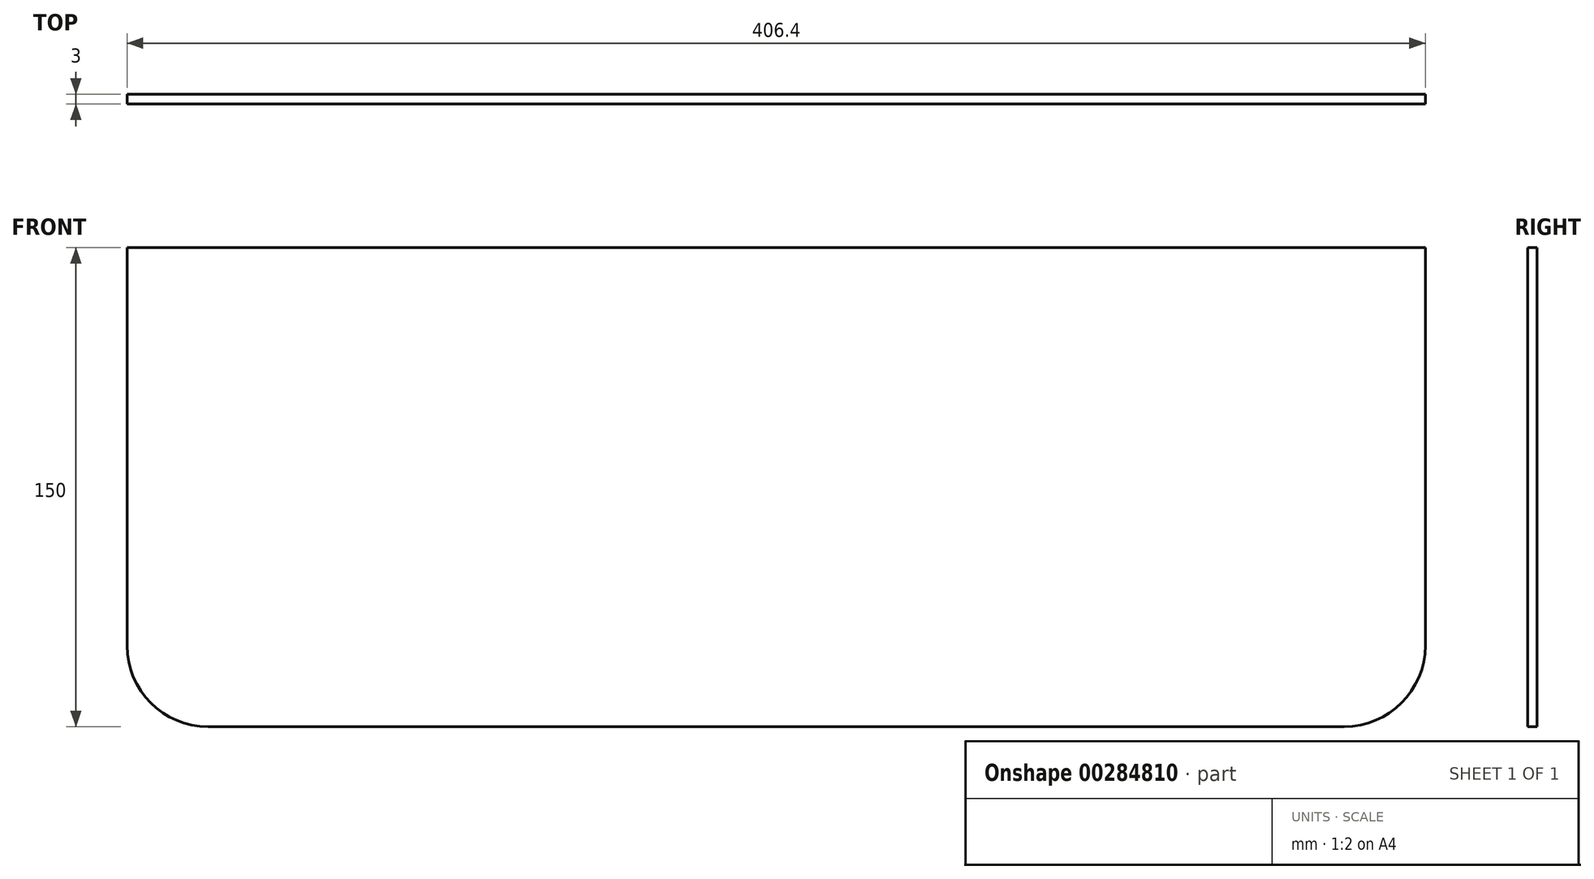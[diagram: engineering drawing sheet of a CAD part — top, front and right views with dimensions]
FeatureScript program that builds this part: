
annotation { "Feature Type Name" : "Feature", "Feature Type Description" : "" }
export const myFeature = defineFeature(function(context is Context, id is Id, definition is map)
    precondition{}
    {
        {
            var Q0;
            Q0=qCreatedBy(makeId("Front.planeOp"),FACE);
            var sketch = newSketch(context, id + "F0", { "sketchPlane" : qUnion([Q0])});
            skLineSegment(sketch, "E0.bottom", {"start": v(181.97, 93.48) * mm, "end": v(-224.43, 93.48) * mm});
            skLineSegment(sketch, "E0.top", {"start": v(156.57, -56.52) * mm, "end": v(-199.03, -56.52) * mm});
            skLineSegment(sketch, "E0.left", {"start": v(181.97, 93.48) * mm, "end": v(181.97, -31.12) * mm});
            skLineSegment(sketch, "E0.right", {"start": v(-224.43, 93.48) * mm, "end": v(-224.43, -31.12) * mm});
            skPoint(sketch, "E1.visualSharp", {"position": v(181.97, -56.52) * mm});
            skArc(sketch, "E1.filletArc", {"start": v(156.57, -56.52) * mm, "mid": v(174.53, -49.08) * mm, "end": v(181.97, -31.12) * mm});
            skPoint(sketch, "E2.visualSharp", {"position": v(-224.43, -56.52) * mm});
            skArc(sketch, "E2.filletArc", {"start": v(-224.43, -31.12) * mm, "mid": v(-216.99, -49.08) * mm, "end": v(-199.03, -56.52) * mm});
            skSolve(sketch);
        }
        {
            var Q0;
            Q0=makeQuery(id+"F0.imprint","IMPRINT",FACE,{"disambiguationData":[TD([[makeQuery(id+"F0.imprint","IMPRINT",EDGE,{"derivedFrom":sQuery(id+"F0.wireOp",EDGE,"E0.bottom")}),1.0]])]});
            extrude(context, id + "F1", {"entities" : qUnion([Q0]), "depth" : 3 * mm});
        }
    });
